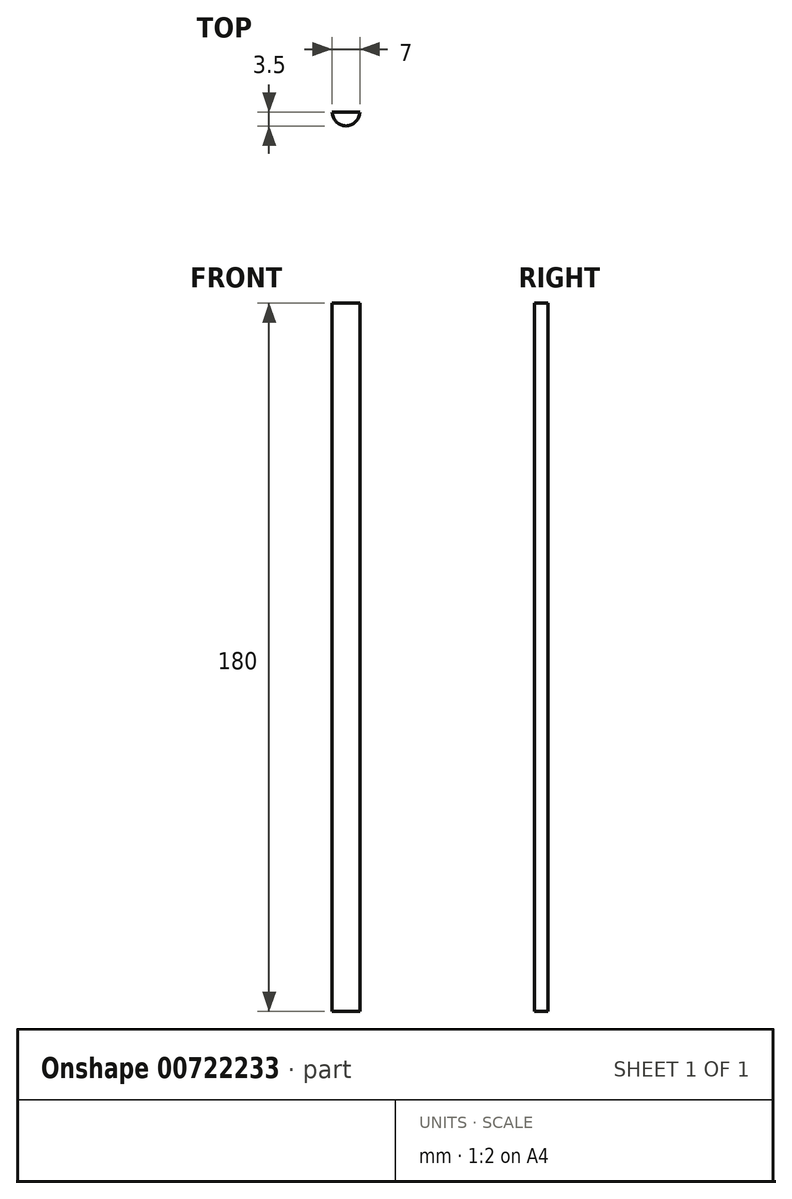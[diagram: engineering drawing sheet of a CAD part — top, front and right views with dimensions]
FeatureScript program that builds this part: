
annotation { "Feature Type Name" : "Feature", "Feature Type Description" : "" }
export const myFeature = defineFeature(function(context is Context, id is Id, definition is map)
    precondition{}
    {
        {
            var Q0;
            Q0=qCreatedBy(makeId("Top.planeOp"),FACE);
            var sketch = newSketch(context, id + "F0", { "sketchPlane" : qUnion([Q0])});
            skLineSegment(sketch, "E0", {"start": v(0, 60) * mm, "end": v(0, -60) * mm});
            skLineSegment(sketch, "E1", {"start": v(-70, 0) * mm, "end": v(70, 0) * mm});
            skCircle(sketch, "E2", {"center": v(0, 0) * mm, "radius": 3.5 * mm});
            skCircle(sketch, "E3", {"center": v(0, 0) * mm, "radius": 1.27 * mm});
            skSolve(sketch);
        }
        {
            var Q0;
            {var subQ0=sQuery(id+"F0.wireOp",EDGE,"E3");var subQ1=sQuery(id+"F0.wireOp",EDGE,"E0");var subQ2=makeQuery(id+"F0.imprint","INTERSECT",VERTEX,{"disambiguationData":[OD(0.0)],"derivedFrom":[subQ1,subQ0]});Q0=makeQuery(id+"F0.imprint","IMPRINT",FACE,{"disambiguationData":[TD([[makeQuery(id+"F0.imprint","IMPRINT",EDGE,{"disambiguationData":[TD([[subQ2,-1.0]])],"derivedFrom":subQ1}),-1.0]])]});}
            var Q1;
            {var subQ0=sQuery(id+"F0.wireOp",EDGE,"E3");var subQ1=sQuery(id+"F0.wireOp",EDGE,"E0");var subQ2=makeQuery(id+"F0.imprint","INTERSECT",VERTEX,{"disambiguationData":[OD(0.0)],"derivedFrom":[subQ1,subQ0]});Q1=makeQuery(id+"F0.imprint","IMPRINT",FACE,{"disambiguationData":[TD([[makeQuery(id+"F0.imprint","IMPRINT",EDGE,{"disambiguationData":[TD([[subQ2,-1.0]])],"derivedFrom":subQ1}),1.0]])]});}
            var Q2;
            {var subQ0=sQuery(id+"F0.wireOp",EDGE,"E1");var subQ1=sQuery(id+"F0.wireOp",EDGE,"E0");var subQ2=makeQuery(id+"F0.imprint","INTERSECT",VERTEX,{"derivedFrom":[subQ1,subQ0]});Q2=makeQuery(id+"F0.imprint","IMPRINT",FACE,{"disambiguationData":[TD([[makeQuery(id+"F0.imprint","IMPRINT",EDGE,{"disambiguationData":[TD([[subQ2,-1.0]])],"derivedFrom":subQ1}),1.0]])]});}
            var Q3;
            {var subQ0=sQuery(id+"F0.wireOp",EDGE,"E1");var subQ1=sQuery(id+"F0.wireOp",EDGE,"E0");var subQ2=makeQuery(id+"F0.imprint","INTERSECT",VERTEX,{"derivedFrom":[subQ1,subQ0]});Q3=makeQuery(id+"F0.imprint","IMPRINT",FACE,{"disambiguationData":[TD([[makeQuery(id+"F0.imprint","IMPRINT",EDGE,{"disambiguationData":[TD([[subQ2,-1.0]])],"derivedFrom":subQ1}),-1.0]])]});}
            extrude(context, id + "F1", {"entities" : qUnion([Q0, Q1, Q2, Q3]), "depth" : 180 * mm, "offsetDistance" : 25 * mm});
        }
    });
